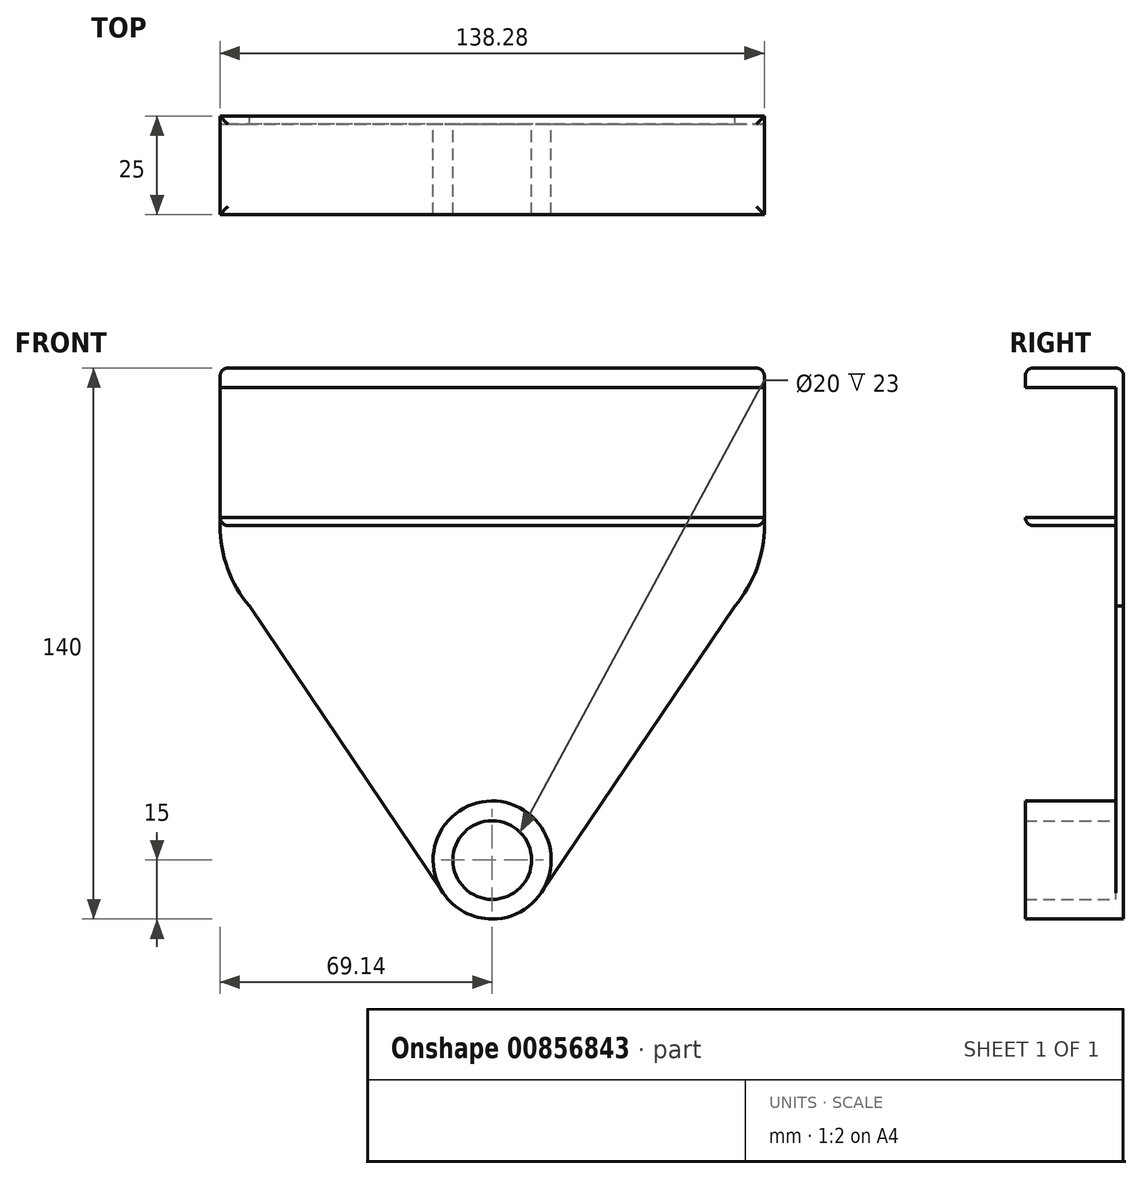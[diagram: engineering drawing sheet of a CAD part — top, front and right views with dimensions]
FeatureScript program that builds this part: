
annotation { "Feature Type Name" : "Feature", "Feature Type Description" : "" }
export const myFeature = defineFeature(function(context is Context, id is Id, definition is map)
    precondition{}
    {
        {
            var Q0;
            Q0=qCreatedBy(makeId("Front.planeOp"),FACE);
            var sketch = newSketch(context, id + "F0", { "sketchPlane" : qUnion([Q0])});
            skLineSegment(sketch, "E0.bottom", {"start": v(69.14, -20) * mm, "end": v(-69.14, -20) * mm});
            skLineSegment(sketch, "E0.top", {"start": v(69.14, 20) * mm, "end": v(-69.14, 20) * mm});
            skLineSegment(sketch, "E0.left", {"start": v(69.14, -20) * mm, "end": v(69.14, 20) * mm});
            skLineSegment(sketch, "E0.right", {"start": v(-69.14, -20) * mm, "end": v(-69.14, 20) * mm});
            skPoint(sketch, "E0.middle", {"position": v(0, 0) * mm});
            skLineSegment(sketch, "E1", {"start": v(0, -20) * mm, "end": v(0, -137.9) * mm, "construction": true});
            skLineSegment(sketch, "E2", {"start": v(-69.14, 15) * mm, "end": v(69.14, 15) * mm});
            skLineSegment(sketch, "E3", {"start": v(-69.14, -18) * mm, "end": v(69.14, -18) * mm});
            skCircle(sketch, "E4", {"center": v(0, -105) * mm, "radius": 15 * mm});
            skLineSegment(sketch, "E5", {"start": v(-12.43, -113.4) * mm, "end": v(-61.67, -40.5) * mm});
            skArc(sketch, "E6", {"start": v(-69.14, -20) * mm, "mid": v(-67.22, -30.9) * mm, "end": v(-61.67, -40.5) * mm});
            skArc(sketch, "E7.MirrorCS", {"start": v(69.14, -20) * mm, "mid": v(67.22, -30.9) * mm, "end": v(61.67, -40.5) * mm});
            skLineSegment(sketch, "E8.MirrorCS", {"start": v(12.43, -113.4) * mm, "end": v(61.67, -40.5) * mm});
            skPoint(sketch, "E9", {"position": v(0, -120) * mm});
            skCircle(sketch, "E10.0", {"center": v(0, -105) * mm, "radius": 10 * mm});
            skSolve(sketch);
        }
        {
            var Q0;
            Q0=makeQuery(id+"F0.imprint","IMPRINT",FACE,{"disambiguationData":[TD([[makeQuery(id+"F0.imprint","IMPRINT",EDGE,{"derivedFrom":sQuery(id+"F0.wireOp",EDGE,"E0.bottom")}),1.0]])]});
            var Q1;
            {var subQ0=sQuery(id+"F0.wireOp",EDGE,"E2");Q1=makeQuery(id+"F0.imprint","IMPRINT",FACE,{"disambiguationData":[TD([[makeQuery(id+"F0.imprint","IMPRINT",EDGE,{"derivedFrom":subQ0}),-1.0]])]});}
            var Q2;
            Q2=makeQuery(id+"F0.imprint","IMPRINT",FACE,{"disambiguationData":[TD([[makeQuery(id+"F0.imprint","IMPRINT",EDGE,{"derivedFrom":sQuery(id+"F0.wireOp",EDGE,"E10.0")}),1.0]])]});
            var Q3;
            Q3=makeQuery(id+"F0.imprint","IMPRINT",FACE,{"disambiguationData":[TD([[makeQuery(id+"F0.imprint","IMPRINT",EDGE,{"derivedFrom":sQuery(id+"F0.wireOp",EDGE,"E10.0")}),-1.0]])]});
            var Q4;
            {var subQ0=sQuery(id+"F0.wireOp",EDGE,"E0.top");Q4=makeQuery(id+"F0.imprint","IMPRINT",FACE,{"disambiguationData":[TD([[makeQuery(id+"F0.imprint","IMPRINT",EDGE,{"derivedFrom":subQ0}),1.0]])]});}
            var Q5;
            {var subQ0=sQuery(id+"F0.wireOp",EDGE,"E0.bottom");Q5=makeQuery(id+"F0.imprint","IMPRINT",FACE,{"disambiguationData":[TD([[makeQuery(id+"F0.imprint","IMPRINT",EDGE,{"derivedFrom":subQ0}),-1.0]])]});}
            extrude(context, id + "F1", {"entities" : qUnion([Q0, Q1, Q2, Q3, Q4, Q5]), "depth" : 2 * mm, "offsetDistance" : 25 * mm});
        }
        {
            var Q0;
            {var subQ0=sQuery(id+"F0.wireOp",EDGE,"E0.top");Q0=makeQuery(id+"F0.imprint","IMPRINT",FACE,{"disambiguationData":[TD([[makeQuery(id+"F0.imprint","IMPRINT",EDGE,{"derivedFrom":subQ0}),1.0]])]});}
            var Q1;
            {var subQ0=sQuery(id+"F0.wireOp",EDGE,"E0.bottom");Q1=makeQuery(id+"F0.imprint","IMPRINT",FACE,{"disambiguationData":[TD([[makeQuery(id+"F0.imprint","IMPRINT",EDGE,{"derivedFrom":subQ0}),-1.0]])]});}
            var Q2;
            Q2=makeQuery(id+"F0.imprint","IMPRINT",FACE,{"disambiguationData":[TD([[makeQuery(id+"F0.imprint","IMPRINT",EDGE,{"derivedFrom":sQuery(id+"F0.wireOp",EDGE,"E10.0")}),-1.0]])]});
            extrude(context, id + "F2", {"entities" : qUnion([Q0, Q1, Q2]), "operationType" : NewBodyOperationType.ADD, "depth" : 25 * mm, "offsetDistance" : 25 * mm});
        }
        {
            var Q0;
            {var subQ0=sQuery(id+"F0.wireOp",EDGE,"E0.top");Q0=makeQuery(id+"F2.boolean.opBoolean","MERGE",FACE,{"derivedFrom":[makeQuery(id+"F1.opExtrude","SWEPT_FACE",FACE,{"disambiguationData":[OSD([subQ0])]}),makeQuery(id+"F2.opExtrude","SWEPT_FACE",FACE,{"disambiguationData":[OSD([subQ0])]})]});}
            var Q1;
            Q1=makeQuery(id+"F2.opExtrude","CAP_EDGE",EDGE,{"disambiguationData":[OSD([sQuery(id+"F0.wireOp",EDGE,"E0.bottom")])],"isStart":false});
            var Q2;
            Q2=makeQuery(id+"F2.opExtrude","SWEPT_EDGE",EDGE,{"disambiguationData":[OSD([sQuery(id+"F0.wireOp",EDGE,"E0.bottom"),sQuery(id+"F0.wireOp",EDGE,"E0.left"),sQuery(id+"F0.wireOp",EDGE,"E7.MirrorCS")])]});
            var Q3;
            Q3=makeQuery(id+"F2.opExtrude","SWEPT_EDGE",EDGE,{"disambiguationData":[OSD([sQuery(id+"F0.wireOp",EDGE,"E0.bottom"),sQuery(id+"F0.wireOp",EDGE,"E0.right"),sQuery(id+"F0.wireOp",EDGE,"E6")])]});
            fillet(context, id + "F3", {"entities" : qUnion([Q0, Q1, Q2, Q3]), "tangentPropagation" : true, "radius" : 2 * mm, "defaultsChanged" : false, "vertexSettings" : [], "allowEdgeOverflow" : false});
        }
    });
